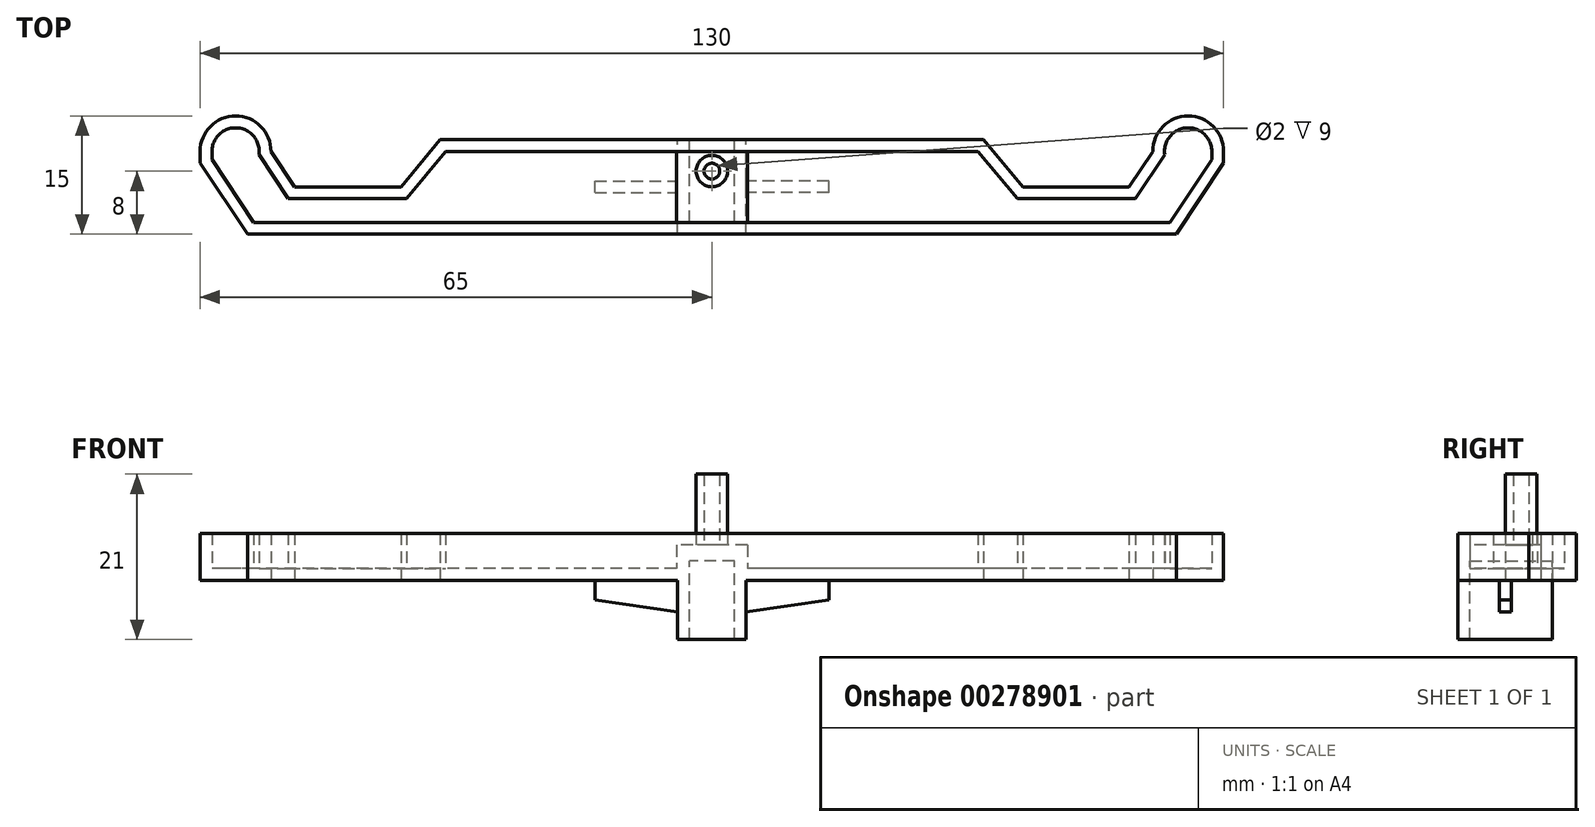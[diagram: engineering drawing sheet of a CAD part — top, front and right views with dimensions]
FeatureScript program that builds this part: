
annotation { "Feature Type Name" : "Feature", "Feature Type Description" : "" }
export const myFeature = defineFeature(function(context is Context, id is Id, definition is map)
    precondition{}
    {
        {
            var Q0;
            Q0=qCreatedBy(makeId("Top.planeOp"),FACE);
            var sketch = newSketch(context, id + "F0", { "sketchPlane" : qUnion([Q0])});
            skLineSegment(sketch, "E0.right", {"start": v(-65, 6) * mm, "end": v(-65, -6) * mm});
            skPoint(sketch, "E0.middle", {"position": v(0, 0) * mm});
            skLineSegment(sketch, "E1", {"start": v(0, -6) * mm, "end": v(0, 6) * mm});
            skLineSegment(sketch, "E2", {"start": v(-59, -6) * mm, "end": v(-65, 3) * mm});
            skLineSegment(sketch, "E3", {"start": v(0, 6) * mm, "end": v(-65, 6) * mm});
            skLineSegment(sketch, "E4", {"start": v(0, -6) * mm, "end": v(-65, -6) * mm});
            skLineSegment(sketch, "E5", {"start": v(-65, 4.5) * mm, "end": v(0, 4.5) * mm, "construction": true});
            skCircle(sketch, "E6", {"center": v(-60.5, 4.5) * mm, "radius": 4.5 * mm});
            skLineSegment(sketch, "E7", {"start": v(-65, 0) * mm, "end": v(0, 0) * mm, "construction": true});
            skLineSegment(sketch, "E8", {"start": v(-56, 4.5) * mm, "end": v(-53, 0) * mm});
            skLineSegment(sketch, "E9", {"start": v(-53, 0) * mm, "end": v(-39.5, 0) * mm});
            skLineSegment(sketch, "E10", {"start": v(-39.5, 0) * mm, "end": v(-34.5, 6) * mm});
            skSolve(sketch);
        }
        {
            var Q0;
            Q0=makeQuery(id+"F0.imprint","IMPRINT",FACE,{"disambiguationData":[TD([[makeQuery(id+"F0.imprint","IMPRINT",EDGE,{"derivedFrom":sQuery(id+"F0.wireOp",EDGE,"E0.bottom")}),1.0]])]});
            var Q1;
            {var subQ2=sQuery(id+"F0.wireOp",EDGE,"E1");Q1=makeQuery(id+"F0.imprint","IMPRINT",FACE,{"disambiguationData":[TD([[makeQuery(id+"F0.imprint","IMPRINT",EDGE,{"derivedFrom":subQ2}),1.0]])]});}
            var Q2;
            {var subQ0=sQuery(id+"F0.wireOp",EDGE,"E6");var subQ1=sQuery(id+"F0.wireOp",EDGE,"E3");var subQ2=makeQuery(id+"F0.imprint","INTERSECT",VERTEX,{"disambiguationData":[OD(0.0)],"derivedFrom":[subQ1,subQ0]});Q2=makeQuery(id+"F0.imprint","IMPRINT",FACE,{"disambiguationData":[TD([[makeQuery(id+"F0.imprint","IMPRINT",EDGE,{"disambiguationData":[TD([[subQ2,-1.0]])],"derivedFrom":subQ1}),1.0]])]});}
            var Q3;
            {var subQ0=sQuery(id+"F0.wireOp",EDGE,"E6");var subQ1=sQuery(id+"F0.wireOp",EDGE,"E3");var subQ2=makeQuery(id+"F0.imprint","INTERSECT",VERTEX,{"disambiguationData":[OD(0.0)],"derivedFrom":[subQ1,subQ0]});Q3=makeQuery(id+"F0.imprint","IMPRINT",FACE,{"disambiguationData":[TD([[makeQuery(id+"F0.imprint","IMPRINT",EDGE,{"disambiguationData":[TD([[subQ2,-1.0]])],"derivedFrom":subQ1}),-1.0]])]});}
            extrude(context, id + "F1", {"entities" : qUnion([Q0, Q1, Q2, Q3]), "depth" : 6 * mm});
        }
        {
            var Q0;
            Q0=makeQuery(id+"F1.opExtrude","SWEPT_BODY",BODY,{"disambiguationData":[OSD([sQuery(id+"F0.wireOp",EDGE,"E0.right"),sQuery(id+"F0.wireOp",EDGE,"E1"),sQuery(id+"F0.wireOp",EDGE,"E2"),sQuery(id+"F0.wireOp",EDGE,"E3"),sQuery(id+"F0.wireOp",EDGE,"E4"),sQuery(id+"F0.wireOp",EDGE,"E6"),sQuery(id+"F0.wireOp",EDGE,"E8"),sQuery(id+"F0.wireOp",EDGE,"E9"),sQuery(id+"F0.wireOp",EDGE,"E10")])]});
            var Q1;
            Q1=qCreatedBy(makeId("Right.planeOp"),FACE);
            mirror(context, id + "F2", {"operationType" : NewBodyOperationType.ADD, "entities" : qUnion([Q0]), "mirrorPlane" : qUnion([Q1])});
        }
        {
            var Q0;
            Q0=makeQuery(id+"F1.opExtrude","CAP_FACE",FACE,{"disambiguationData":[OSD([sQuery(id+"F0.wireOp",EDGE,"E0.bottom"),sQuery(id+"F0.wireOp",EDGE,"E0.top"),sQuery(id+"F0.wireOp",EDGE,"E0.left"),sQuery(id+"F0.wireOp",EDGE,"E0.right")])],"isStart":false});
            shell(context, id + "F3", {"entities" : qUnion([Q0]), "thickness" : 1.5 * mm});
        }
        {
            var Q0;
            Q0=makeQuery(id+"F3.opShell","OFFSET_FACE",FACE,{"disambiguationData":[OSD([sQuery(id+"F0.wireOp",EDGE,"E0.right"),sQuery(id+"F0.wireOp",EDGE,"E1"),sQuery(id+"F0.wireOp",EDGE,"E2"),sQuery(id+"F0.wireOp",EDGE,"E3"),sQuery(id+"F0.wireOp",EDGE,"E4"),sQuery(id+"F0.wireOp",EDGE,"E6"),sQuery(id+"F0.wireOp",EDGE,"E8"),sQuery(id+"F0.wireOp",EDGE,"E9"),sQuery(id+"F0.wireOp",EDGE,"E10")])]});
            var sketch = newSketch(context, id + "F4", { "sketchPlane" : qUnion([Q0])});
            skCircle(sketch, "E11", {"center": v(-60.5, 4.5) * mm, "radius": 3 * mm});
            skCircle(sketch, "E12", {"center": v(60.5, 4.5) * mm, "radius": 3 * mm});
            skCircle(sketch, "E13", {"center": v(-60.5, 4.5) * mm, "radius": 1 * mm});
            skCircle(sketch, "E14", {"center": v(60.5, 4.5) * mm, "radius": 1 * mm});
            skSolve(sketch);
        }
        {
            var Q0;
            {var subQ0=sQuery(id+"F4.wireOp",EDGE,"E11");var subQ1=sQuery(id+"F0.wireOp",EDGE,"E8");var subQ2=makeQuery(id+"F4.imprint","INTERSECT",VERTEX,{"derivedFrom":[makeQuery(id+"F3.opShell","OFFSET_EDGE",EDGE,{"disambiguationData":[OSD([subQ1]),TDD([makeQuery(id+"F1.opExtrude","CAP_EDGE",EDGE,{"disambiguationData":[OSD([subQ1])],"isStart":true})])]}),subQ0]});Q0=makeQuery(id+"F4.imprint","IMPRINT",FACE,{"disambiguationData":[TD([[makeQuery(id+"F4.imprint","IMPRINT",EDGE,{"disambiguationData":[TD([[subQ2,1.0]])],"derivedFrom":subQ0}),1.0]])]});}
            var Q1;
            {var subQ0=sQuery(id+"F4.wireOp",EDGE,"E12");Q1=makeQuery(id+"F4.imprint","IMPRINT",FACE,{"disambiguationData":[TD([[makeQuery(id+"F4.imprint","IMPRINT",EDGE,{"disambiguationData":[OD(0.0)],"derivedFrom":subQ0}),1.0]])]});}
            extrude(context, id + "F5", {"entities" : qUnion([Q0, Q1]), "operationType" : NewBodyOperationType.REMOVE, "depth" : 26 * mm, "offsetDistance" : 25 * mm});
        }
        {
            var Q0;
            {var subQ0=sQuery(id+"F0.wireOp",EDGE,"E9");var subQ2=sQuery(id+"F0.wireOp",EDGE,"E8");var subQ4=sQuery(id+"F0.wireOp",EDGE,"E2");var subQ6=sQuery(id+"F0.wireOp",EDGE,"E0.right");var subQ8=sQuery(id+"F0.wireOp",EDGE,"E10");var subQ10=sQuery(id+"F0.wireOp",EDGE,"E3");var subQ11=sQuery(id+"F0.wireOp",EDGE,"E4");Q0=makeQuery(id+"F5.boolean.opBoolean","SPLIT",FACE,{"disambiguationData":[TD([makeQuery(id+"F3.opShell","OFFSET_FACE",FACE,{"disambiguationData":[OSD([subQ10])]})])],"derivedFrom":makeQuery(id+"F3.opShell","OFFSET_FACE",FACE,{"disambiguationData":[OSD([subQ6,sQuery(id+"F0.wireOp",EDGE,"E1"),subQ4,subQ10,subQ11,sQuery(id+"F0.wireOp",EDGE,"E6"),subQ2,subQ0,subQ8])]})});}
            var sketch = newSketch(context, id + "F6", { "sketchPlane" : qUnion([Q0])});
            skLineSegment(sketch, "E15.bottom", {"start": v(4.5, 4.5) * mm, "end": v(-4.5, 4.5) * mm});
            skLineSegment(sketch, "E15.top", {"start": v(4.5, -4.5) * mm, "end": v(-4.5, -4.5) * mm});
            skLineSegment(sketch, "E15.left", {"start": v(4.5, 4.5) * mm, "end": v(4.5, -4.5) * mm});
            skLineSegment(sketch, "E15.right", {"start": v(-4.5, 4.5) * mm, "end": v(-4.5, -4.5) * mm});
            skPoint(sketch, "E15.middle", {"position": v(0, 0) * mm});
            skSolve(sketch);
        }
        {
            var Q0;
            Q0=makeQuery(id+"F6.imprint","IMPRINT",FACE,{"disambiguationData":[TD([[makeQuery(id+"F6.imprint","IMPRINT",EDGE,{"derivedFrom":sQuery(id+"F6.wireOp",EDGE,"E15.bottom")}),1.0]])]});
            extrude(context, id + "F7", {"entities" : qUnion([Q0]), "operationType" : NewBodyOperationType.ADD, "depth" : 3 * mm});
        }
        {
            var Q0;
            Q0=makeQuery(id+"F7.opExtrude","CAP_FACE",FACE,{"disambiguationData":[OSD([sQuery(id+"F6.wireOp",EDGE,"E15.bottom"),sQuery(id+"F6.wireOp",EDGE,"E15.top"),sQuery(id+"F6.wireOp",EDGE,"E15.left"),sQuery(id+"F6.wireOp",EDGE,"E15.right")])],"isStart":false});
            var sketch = newSketch(context, id + "F8", { "sketchPlane" : qUnion([Q0])});
            skCircle(sketch, "E16", {"center": v(0, 2) * mm, "radius": 2 * mm});
            skCircle(sketch, "E17", {"center": v(0, 2) * mm, "radius": 1 * mm});
            skSolve(sketch);
        }
        {
            var Q0;
            Q0=makeQuery(id+"F8.imprint","IMPRINT",FACE,{"disambiguationData":[TD([[makeQuery(id+"F8.imprint","IMPRINT",EDGE,{"derivedFrom":sQuery(id+"F8.wireOp",EDGE,"E16")}),1.0]])]});
            extrude(context, id + "F9", {"entities" : qUnion([Q0]), "operationType" : NewBodyOperationType.ADD, "depth" : 9 * mm});
        }
        {
            var Q0;
            {var subQ0=makeQuery(id+"F1.opExtrude","CAP_FACE",FACE,{"disambiguationData":[OSD([sQuery(id+"F0.wireOp",EDGE,"E0.right"),sQuery(id+"F0.wireOp",EDGE,"E1"),sQuery(id+"F0.wireOp",EDGE,"E2"),sQuery(id+"F0.wireOp",EDGE,"E3"),sQuery(id+"F0.wireOp",EDGE,"E4"),sQuery(id+"F0.wireOp",EDGE,"E6"),sQuery(id+"F0.wireOp",EDGE,"E8"),sQuery(id+"F0.wireOp",EDGE,"E9"),sQuery(id+"F0.wireOp",EDGE,"E10")])],"isStart":true});Q0=makeQuery(id+"F2.boolean.opBoolean","MERGE",FACE,{"derivedFrom":[subQ0,makeQuery(id+"F2.opPattern","COPY",FACE,{"derivedFrom":subQ0,"instanceName":"1"})]});}
            var sketch = newSketch(context, id + "F10", { "sketchPlane" : qUnion([Q0])});
            skLineSegment(sketch, "E18.bottom", {"start": v(-4.35, 6) * mm, "end": v(4.35, 6) * mm});
            skLineSegment(sketch, "E18.top", {"start": v(-4.35, -6) * mm, "end": v(4.35, -6) * mm});
            skLineSegment(sketch, "E18.left", {"start": v(-4.35, 6) * mm, "end": v(-4.35, -6) * mm});
            skLineSegment(sketch, "E18.right", {"start": v(4.35, 6) * mm, "end": v(4.35, -6) * mm});
            skPoint(sketch, "E18.middle", {"position": v(0, 0) * mm});
            skLineSegment(sketch, "E19.0", {"start": v(-2.85, 4.5) * mm, "end": v(-2.85, -6) * mm});
            skLineSegment(sketch, "E19.1", {"start": v(-2.85, 4.5) * mm, "end": v(2.85, 4.5) * mm});
            skLineSegment(sketch, "E19.2", {"start": v(2.85, 4.5) * mm, "end": v(2.85, -6) * mm});
            skSolve(sketch);
        }
        {
            var Q0;
            Q0=makeQuery(id+"F10.imprint","IMPRINT",FACE,{"disambiguationData":[TD([[makeQuery(id+"F10.imprint","IMPRINT",EDGE,{"derivedFrom":sQuery(id+"F10.wireOp",EDGE,"E18.bottom")}),1.0]])]});
            extrude(context, id + "F11", {"entities" : qUnion([Q0]), "operationType" : NewBodyOperationType.ADD, "depth" : 7.5 * mm});
        }
        {
            var Q0;
            {var subQ1=sQuery(id+"F0.wireOp",EDGE,"E3");var subQ6=sQuery(id+"F10.wireOp",EDGE,"E19.0");var subQ7=makeQuery(id+"F1.opExtrude","CAP_FACE",FACE,{"disambiguationData":[OSD([sQuery(id+"F0.wireOp",EDGE,"E0.right"),sQuery(id+"F0.wireOp",EDGE,"E1"),sQuery(id+"F0.wireOp",EDGE,"E2"),subQ1,sQuery(id+"F0.wireOp",EDGE,"E4"),sQuery(id+"F0.wireOp",EDGE,"E6"),sQuery(id+"F0.wireOp",EDGE,"E8"),sQuery(id+"F0.wireOp",EDGE,"E9"),sQuery(id+"F0.wireOp",EDGE,"E10")])],"isStart":true});Q0=makeQuery(id+"F11.boolean.opBoolean","SPLIT",FACE,{"disambiguationData":[TD([makeQuery(id+"F11.opExtrude","SWEPT_FACE",FACE,{"disambiguationData":[OSD([subQ6])]})])],"derivedFrom":makeQuery(id+"F2.boolean.opBoolean","MERGE",FACE,{"derivedFrom":[subQ7,makeQuery(id+"F2.opPattern","COPY",FACE,{"derivedFrom":subQ7,"instanceName":"1"})]})});}
            extrude(context, id + "F12", {"entities" : qUnion([Q0]), "operationType" : NewBodyOperationType.REMOVE, "oppositeDirection" : true, "depth" : 2.5 * mm});
        }
        {
            var Q0;
            Q0=qCreatedBy(makeId("Front.planeOp"),FACE);
            var sketch = newSketch(context, id + "F13", { "sketchPlane" : qUnion([Q0])});
            skLineSegment(sketch, "E20.0", {"start": v(4.35, -4) * mm, "end": v(4.35, 0) * mm});
            skLineSegment(sketch, "E21.0", {"start": v(14.85, 0) * mm, "end": v(4.35, 0) * mm});
            skLineSegment(sketch, "E22", {"start": v(14.85, 0) * mm, "end": v(14.85, -2.5) * mm});
            skLineSegment(sketch, "E23", {"start": v(14.85, -2.5) * mm, "end": v(4.35, -4) * mm});
            skLineSegment(sketch, "E24", {"start": v(0, 0) * mm, "end": v(0, -9.9) * mm, "construction": true});
            skPoint(sketch, "E25.orphan", {"position": v(4.35, -7.5) * mm});
            skPoint(sketch, "E26.orphan", {"position": v(34.5, 0) * mm});
            skLineSegment(sketch, "E27.MirrorCS", {"start": v(-4.35, -4) * mm, "end": v(-4.35, 0) * mm});
            skPoint(sketch, "E28.MirrorP", {"position": v(-4.35, -7.5) * mm});
            skLineSegment(sketch, "E29.MirrorCS", {"start": v(-14.85, -2.5) * mm, "end": v(-4.35, -4) * mm});
            skLineSegment(sketch, "E30.MirrorCS", {"start": v(-14.85, 0) * mm, "end": v(-4.35, 0) * mm});
            skLineSegment(sketch, "E31.MirrorCS", {"start": v(-14.85, 0) * mm, "end": v(-14.85, -2.5) * mm});
            skSolve(sketch);
        }
        {
            var Q0;
            Q0=makeQuery(id+"F13.imprint","IMPRINT",FACE,{"disambiguationData":[TD([[makeQuery(id+"F13.imprint","IMPRINT",EDGE,{"derivedFrom":sQuery(id+"F13.wireOp",EDGE,"E20.0")}),-1.0]])]});
            var Q1;
            Q1=makeQuery(id+"F13.imprint","IMPRINT",FACE,{"disambiguationData":[TD([[makeQuery(id+"F13.imprint","IMPRINT",EDGE,{"derivedFrom":sQuery(id+"F13.wireOp",EDGE,"E27.MirrorCS")}),1.0]])]});
            extrude(context, id + "F14", {"entities" : qUnion([Q0, Q1]), "operationType" : NewBodyOperationType.ADD, "endBound" : BoundingType.SYMMETRIC, "depth" : 1.5 * mm});
        }
    });
